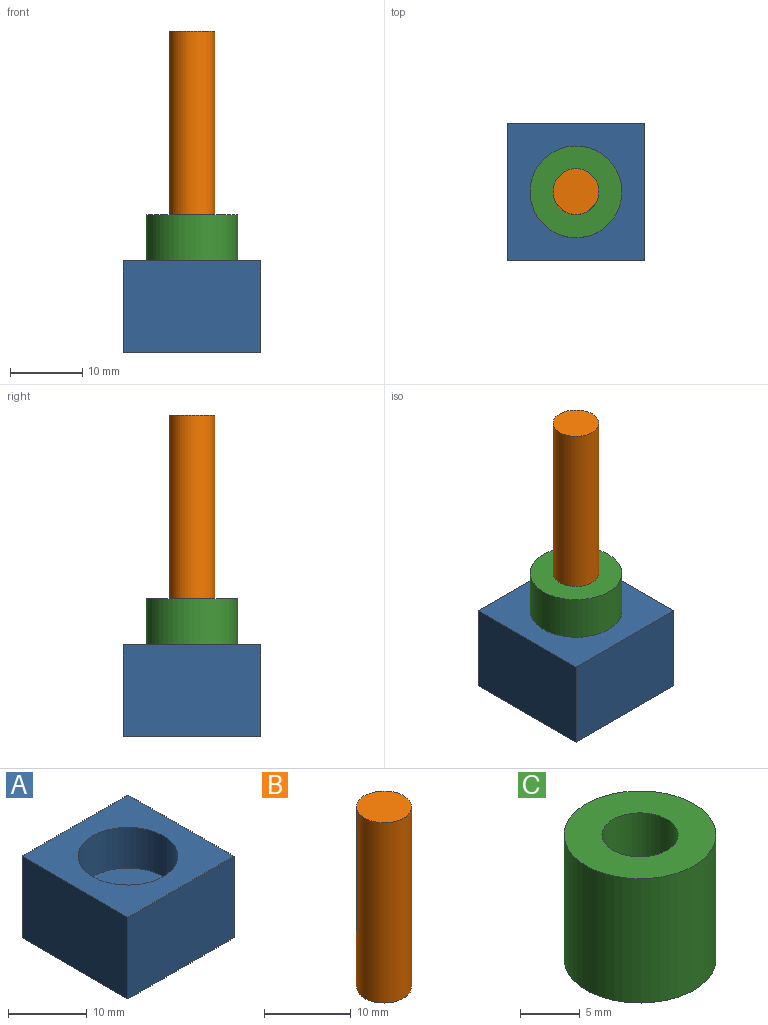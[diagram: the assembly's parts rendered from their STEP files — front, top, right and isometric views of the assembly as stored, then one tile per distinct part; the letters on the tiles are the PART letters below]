
ASSEMBLY  parts=3 mates=2
PART A: 8 faces, bbox 19.1x19.1x12.7 mm
  f0: plane 19.05x12.7mm, normal (1,0,0), area 241.9mm2, adj f1,f3,f4,f5
  f1: plane 19.05x12.7mm, normal (0,1,0), area 241.9mm2, adj f0,f2,f4,f5
  f2: plane 19.05x12.7mm, normal (-1,0,0), area 241.9mm2, adj f1,f3,f4,f5
  f3: plane 19.05x12.7mm, normal (0,-1,0), area 241.9mm2, adj f0,f2,f4,f5
  f4: plane 19.05x19.05mm, normal (0,0,1), area 236.2mm2, adj f0,f1,f2,f3,f6
  f5: plane 19.05x19.05mm, normal (0,0,-1), area 362.9mm2, adj f0,f1,f2,f3
  f6: cylinder r=6.35mm len=12.7mm, axis (0,0,1), area 253.4mm2, adj f4,f7
  f7: plane 12.7x12.7mm, normal (0,0,1), area 126.7mm2, adj f6
PART B: 3 faces, bbox 6.3x6.3x25.4 mm
  f0: cylinder r=3.17mm len=25.4mm, axis (0,0,-1), area 505.7mm2, adj f1,f2
  f1: plane 6.34x6.34mm, normal (0,0,1), area 31.5mm2, adj f0
  f2: plane 6.34x6.34mm, normal (0,0,-1), area 31.5mm2, adj f0
PART C: 4 faces, bbox 12.7x12.7x12.7 mm
  f0: cylinder r=3.17mm len=12.7mm, axis (0,0,-1), area 253.4mm2, adj f2,f3
  f1: cylinder r=6.34mm len=12.7mm, axis (0,0,-1), area 506.1mm2, adj f2,f3
  f2: plane 12.68x12.68mm, normal (0,0,1), area 94.7mm2, adj f0,f1
  f3: plane 12.68x12.68mm, normal (0,0,-1), area 94.7mm2, adj f0,f1
PLACE A at identity fixed
PLACE B t=(0,0,19.05)mm
PLACE C t=(0,0,6.35)mm
MATE fastened A.f6 <-> C.f0  axis (0,0,1) through (0,0,6.35)mm
MATE fastened B.f0 <-> C.f1  axis (0,0,-1) through (0,0,19.05)mm
